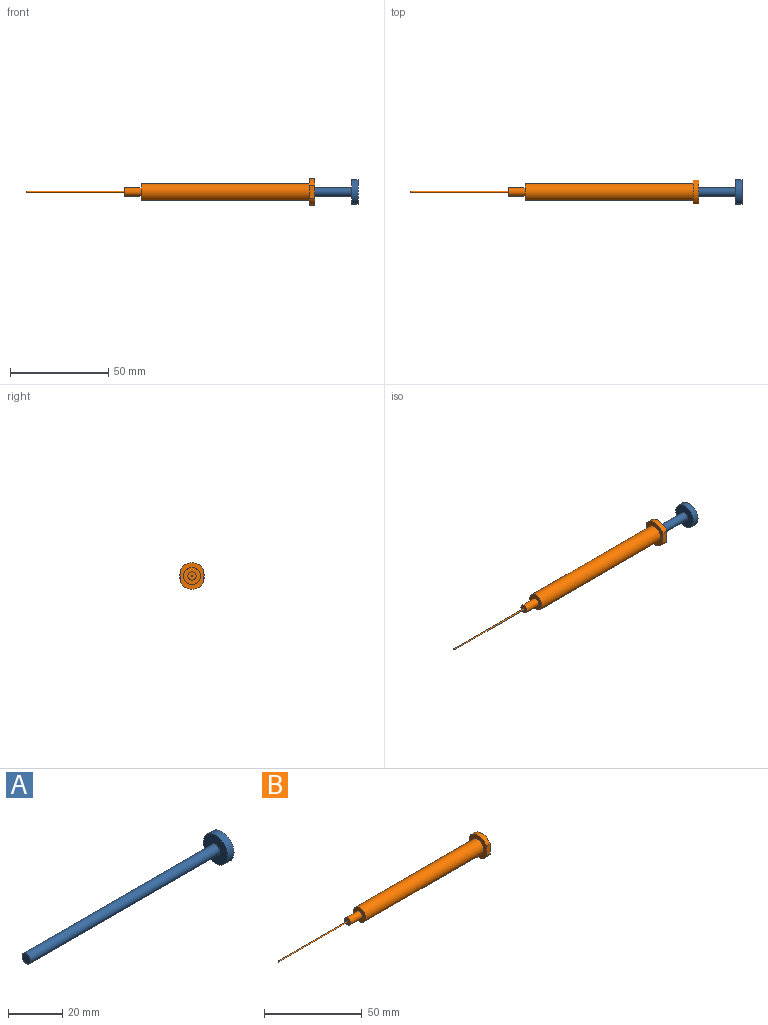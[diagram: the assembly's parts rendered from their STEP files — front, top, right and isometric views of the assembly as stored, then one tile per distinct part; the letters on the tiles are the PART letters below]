
ASSEMBLY  parts=2 mates=1
PART A: 5 faces, bbox 101.7x12.7x12.7 mm
  f0: plane 4.4x4.4mm, normal (-1,0,0), area 15.2mm2, adj f4
  f1: plane 12.7x12.7mm, normal (1,0,0), area 126.7mm2, adj f2
  f2: cylinder r=6.35mm len=12.7mm, axis (1,0,0), area 129.7mm2, adj f1,f3
  f3: plane 12.7x12.7mm, normal (-1,0,0), area 111.5mm2, adj f2,f4
  f4: cylinder r=2.2mm len=98.4mm, axis (1,0,0), area 1360.2mm2, adj f0,f3
PART B: 14 faces, bbox 147x11.9x13.6 mm
  f0: plane 13.6x11.9mm, normal (1,0,0), area 121.8mm2, adj f1,f2,f10,f12,f13
  f1: cylinder r=6.8mm len=11.9mm, axis (-1,0,0), area 40.6mm2, adj f0,f11,f12,f13
  f2: cylinder r=6.8mm len=11.9mm, axis (-1,0,0), area 40.6mm2, adj f0,f11,f12,f13
  f3: cylinder r=4.33mm len=85.6mm, axis (-1,0,0), area 2326.2mm2, adj f4,f11
  f4: plane 8.65x8.65mm, normal (-1,0,0), area 44.9mm2, adj f3,f5
  f5: cylinder r=2.1mm len=8.6mm, axis (-1,0,0), area 113.5mm2, adj f4,f6
  f6: plane 4.2x4.2mm, normal (-1,0,0), area 13.5mm2, adj f5,f7
  f7: cylinder r=0.35mm len=50mm, axis (-1,0,0), area 110mm2, adj f6,f8
  f8: plane 0.7x0.7mm, normal (-1,0,0), area 0.4mm2, adj f7
  f9: plane 4.5x4.5mm, normal (1,0,0), area 15.9mm2, adj f10
  f10: cylinder r=2.25mm len=85.4mm, axis (-1,0,0), area 1207.3mm2, adj f0,f9
  f11: plane 13.6x11.9mm, normal (-1,0,0), area 78.9mm2, adj f1,f2,f3,f12,f13
  f12: plane 6.58x2.8mm, normal (0,1,0), area 18.4mm2, adj f0,f1,f2,f11
  f13: plane 6.58x2.8mm, normal (0,-1,0), area 18.4mm2, adj f0,f1,f2,f11
PLACE A t=(5.88,0,0)mm
PLACE B at identity fixed
MATE slider B.f1 <-> A.f2  axis (1,0,0) through (-42.7,0,0)mm
